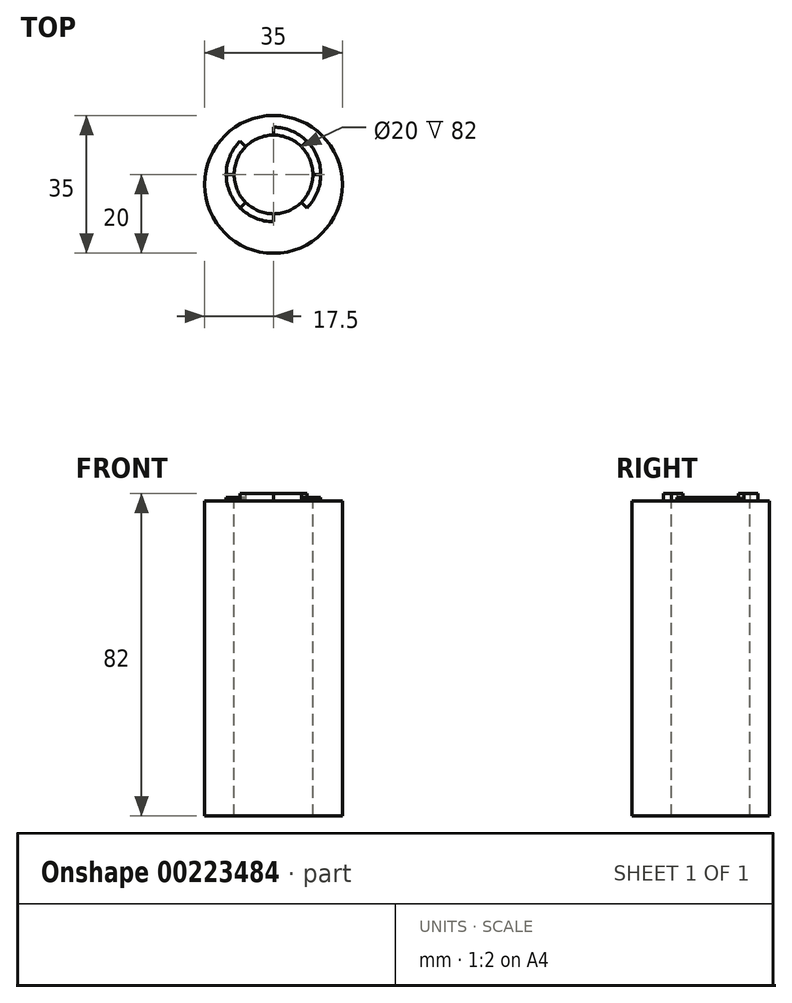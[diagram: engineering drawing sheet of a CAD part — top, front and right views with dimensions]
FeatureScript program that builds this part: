
annotation { "Feature Type Name" : "Feature", "Feature Type Description" : "" }
export const myFeature = defineFeature(function(context is Context, id is Id, definition is map)
    precondition{}
    {
        {
            assignVariable(context, id + "F0", {"name" : "TabDiameter", "anyValue" : 20 * mm});
        }
        {
            assignVariable(context, id + "F1", {"name" : "JigBaseHeight", "anyValue" : 80});
        }
        {
            var Q0;
            Q0=qCreatedBy(makeId("Top.planeOp"),FACE);
            var sketch = newSketch(context, id + "F2", { "sketchPlane" : qUnion([Q0])});
            skCircle(sketch, "E0", {"center": v(0, 0) * mm, "radius": 17.5 * mm});
            skSolve(sketch);
        }
        {
            var Q0;
            Q0 = qSketchRegion(id + "F2", true);
            extrude(context, id + "F3", {"entities" : qUnion([Q0]), "depth" : (getVariable(context, 'JigBaseHeight')) * mm});
        }
        {
            var Q0;
            Q0=makeQuery(id+"F3.opExtrude","CAP_FACE",FACE,{"disambiguationData":[OSD([sQuery(id+"F2.wireOp",EDGE,"E0")])],"isStart":false});
            cPlane(context, id + "F4", {"entities" : qUnion([Q0]), "cplaneType" : CPlaneType.OFFSET, "offset" : 0 * mm, "width" : 150 * mm, "height" : 150 * mm});
        }
        {
            var Q0;
            Q0=qCreatedBy(id+"F4.planeOp",FACE);
            var sketch = newSketch(context, id + "F5", { "sketchPlane" : qUnion([Q0])});
            skPoint(sketch, "E1", {"position": v(0, 2.5) * mm});
            skSolve(sketch);
        }
        {
            var Q0;
            Q0=sQuery(id+"F5.wireOp",VERTEX,"E1");
            var Q1;
            Q1=makeQuery(id+"F3.opExtrude","SWEPT_BODY",BODY,{"disambiguationData":[OSD([sQuery(id+"F2.wireOp",EDGE,"E0")])]});
            hole(context, id + "F6", {"style" : HoleStyle.SIMPLE, "endStyle" : HoleEndStyle.THROUGH, "holeDiameter" : getVariable(context, 'TabDiameter'), "locations" : qUnion([Q0]), "scope" : qUnion([Q1]), "isTappedThrough" : true});
        }
        {
            var Q0;
            Q0=qCreatedBy(id+"F4.planeOp",FACE);
            var sketch = newSketch(context, id + "F7", { "sketchPlane" : qUnion([Q0])});
            skPoint(sketch, "E2", {"position": v(0, 2.5) * mm});
            skArc(sketch, "E3", {"start": v(0, -7.5) * mm, "mid": v(3.83, -6.74) * mm, "end": v(7.07, -4.57) * mm, "construction": true});
            skLineSegment(sketch, "E4", {"start": v(0, -7.5) * mm, "end": v(0, 2.5) * mm, "construction": true});
            skLineSegment(sketch, "E5", {"start": v(7.07, -4.57) * mm, "end": v(0, 2.5) * mm, "construction": true});
            skArc(sketch, "E6", {"start": v(0, -7.5) * mm, "mid": v(-3.83, -6.74) * mm, "end": v(-7.07, -4.57) * mm});
            skLineSegment(sketch, "E7", {"start": v(-7.07, -4.57) * mm, "end": v(0, 2.5) * mm, "construction": true});
            skArc(sketch, "E8", {"start": v(-7.07, -4.57) * mm, "mid": v(-9.24, -1.33) * mm, "end": v(-10, 2.5) * mm, "construction": true});
            skArc(sketch, "E9", {"start": v(-10, 2.5) * mm, "mid": v(-9.24, 6.33) * mm, "end": v(-7.07, 9.57) * mm, "construction": true});
            skArc(sketch, "E10", {"start": v(-7.07, 9.57) * mm, "mid": v(-3.83, 11.74) * mm, "end": v(0, 12.5) * mm, "construction": true});
            skLineSegment(sketch, "E11", {"start": v(0, 2.5) * mm, "end": v(-10, 2.5) * mm, "construction": true});
            skLineSegment(sketch, "E12", {"start": v(0, 2.5) * mm, "end": v(-7.07, 9.57) * mm, "construction": true});
            skLineSegment(sketch, "E13", {"start": v(0, 2.5) * mm, "end": v(0, 12.5) * mm, "construction": true});
            skArc(sketch, "E14", {"start": v(0, 12.5) * mm, "mid": v(3.83, 11.74) * mm, "end": v(7.07, 9.57) * mm});
            skArc(sketch, "E15", {"start": v(7.07, 9.57) * mm, "mid": v(9.24, 6.33) * mm, "end": v(10, 2.5) * mm, "construction": true});
            skLineSegment(sketch, "E16", {"start": v(0, 2.5) * mm, "end": v(7.07, 9.57) * mm, "construction": true});
            skLineSegment(sketch, "E17", {"start": v(0, 2.5) * mm, "end": v(10, 2.5) * mm, "construction": true});
            skArc(sketch, "E18", {"start": v(0, -9.5) * mm, "mid": v(-4.6, -8.59) * mm, "end": v(-8.49, -5.99) * mm});
            skLineSegment(sketch, "E19", {"start": v(-8.49, -5.99) * mm, "end": v(0, 2.5) * mm, "construction": true});
            skLineSegment(sketch, "E20", {"start": v(0, -9.5) * mm, "end": v(0, 2.5) * mm, "construction": true});
            skLineSegment(sketch, "E21", {"start": v(0, 2.5) * mm, "end": v(-8.49, 10.99) * mm, "construction": true});
            skLineSegment(sketch, "E22", {"start": v(0, 2.5) * mm, "end": v(0, 14.43) * mm, "construction": true});
            skLineSegment(sketch, "E23", {"start": v(-8.49, -5.99) * mm, "end": v(-7.07, -4.57) * mm});
            skLineSegment(sketch, "E24", {"start": v(0, -7.5) * mm, "end": v(0, -9.5) * mm});
            skLineSegment(sketch, "E25", {"start": v(-7.07, 9.57) * mm, "end": v(-8.49, 10.99) * mm});
            skLineSegment(sketch, "E26", {"start": v(0, 12.5) * mm, "end": v(0, 14.43) * mm});
            skArc(sketch, "E27", {"start": v(0, 14.5) * mm, "mid": v(4.6, 13.59) * mm, "end": v(8.49, 10.99) * mm});
            skLineSegment(sketch, "E28", {"start": v(0, 14.5) * mm, "end": v(0, 2.5) * mm, "construction": true});
            skLineSegment(sketch, "E29", {"start": v(8.49, 10.99) * mm, "end": v(0, 2.5) * mm, "construction": true});
            skLineSegment(sketch, "E30", {"start": v(0, 14.5) * mm, "end": v(0, 12.5) * mm});
            skLineSegment(sketch, "E31", {"start": v(8.49, 10.99) * mm, "end": v(7.07, 9.57) * mm});
            skSolve(sketch);
        }
        {
            var Q0;
            Q0 = qSketchRegion(id + "F7", true);
            extrude(context, id + "F8", {"entities" : qUnion([Q0]), "operationType" : NewBodyOperationType.ADD, "depth" : 2 * mm});
        }
        {
            var Q0;
            Q0=qCreatedBy(id+"F4.planeOp",FACE);
            var sketch = newSketch(context, id + "F9", { "sketchPlane" : qUnion([Q0])});
            skPoint(sketch, "E32", {"position": v(0, 2.5) * mm});
            skArc(sketch, "E33", {"start": v(0, -7.5) * mm, "mid": v(3.83, -6.74) * mm, "end": v(7.07, -4.57) * mm, "construction": true});
            skLineSegment(sketch, "E34", {"start": v(0, -7.5) * mm, "end": v(0, 2.5) * mm, "construction": true});
            skLineSegment(sketch, "E35", {"start": v(7.07, -4.57) * mm, "end": v(0, 2.5) * mm, "construction": true});
            skArc(sketch, "E36", {"start": v(0, -7.5) * mm, "mid": v(-3.83, -6.74) * mm, "end": v(-7.07, -4.57) * mm});
            skLineSegment(sketch, "E37", {"start": v(-7.07, -4.57) * mm, "end": v(0, 2.5) * mm, "construction": true});
            skArc(sketch, "E38", {"start": v(-7.07, -4.57) * mm, "mid": v(-9.24, -1.33) * mm, "end": v(-10, 2.5) * mm});
            skArc(sketch, "E39", {"start": v(-10, 2.5) * mm, "mid": v(-9.24, 6.33) * mm, "end": v(-7.07, 9.57) * mm});
            skArc(sketch, "E40", {"start": v(-7.07, 9.57) * mm, "mid": v(-3.83, 11.74) * mm, "end": v(0, 12.5) * mm});
            skLineSegment(sketch, "E41", {"start": v(0, 2.5) * mm, "end": v(-10, 2.5) * mm, "construction": true});
            skLineSegment(sketch, "E42", {"start": v(0, 2.5) * mm, "end": v(-7.07, 9.57) * mm, "construction": true});
            skLineSegment(sketch, "E43", {"start": v(0, 2.5) * mm, "end": v(0, 12.5) * mm, "construction": true});
            skArc(sketch, "E44", {"start": v(7.07, 9.57) * mm, "mid": v(9.24, 6.33) * mm, "end": v(10, 2.5) * mm});
            skLineSegment(sketch, "E45", {"start": v(0, 2.5) * mm, "end": v(7.07, 9.57) * mm, "construction": true});
            skLineSegment(sketch, "E46", {"start": v(0, 2.5) * mm, "end": v(10, 2.5) * mm, "construction": true});
            skArc(sketch, "E47", {"start": v(-8.49, -5.99) * mm, "mid": v(-11.09, -2.1) * mm, "end": v(-12, 2.5) * mm});
            skLineSegment(sketch, "E48", {"start": v(-8.49, -5.99) * mm, "end": v(0, 2.5) * mm, "construction": true});
            skLineSegment(sketch, "E49", {"start": v(-12, 2.5) * mm, "end": v(0, 2.5) * mm, "construction": true});
            skLineSegment(sketch, "E50", {"start": v(-8.49, -5.99) * mm, "end": v(-7.07, -4.57) * mm});
            skLineSegment(sketch, "E51", {"start": v(-10, 2.5) * mm, "end": v(-12, 2.5) * mm});
            skPoint(sketch, "E52.startSnap0", {"position": v(-3.54, 6.04) * mm});
            skLineSegment(sketch, "E53", {"start": v(8.43, 10.93) * mm, "end": v(0, 2.5) * mm, "construction": true});
            skLineSegment(sketch, "E54", {"start": v(0, 14.5) * mm, "end": v(0, 2.5) * mm, "construction": true});
            skLineSegment(sketch, "E55", {"start": v(0, 14.5) * mm, "end": v(0, 12.5) * mm});
            skLineSegment(sketch, "E56", {"start": v(7.07, 9.57) * mm, "end": v(8.43, 10.93) * mm});
            skArc(sketch, "E57", {"start": v(8.49, 10.99) * mm, "mid": v(11.09, 7.1) * mm, "end": v(12, 2.5) * mm});
            skLineSegment(sketch, "E58", {"start": v(8.49, 10.99) * mm, "end": v(0, 2.5) * mm, "construction": true});
            skLineSegment(sketch, "E59", {"start": v(12, 2.5) * mm, "end": v(0, 2.5) * mm, "construction": true});
            skLineSegment(sketch, "E60", {"start": v(12, 2.5) * mm, "end": v(10, 2.5) * mm});
            skLineSegment(sketch, "E61", {"start": v(8.49, 10.99) * mm, "end": v(7.07, 9.57) * mm});
            skSolve(sketch);
        }
        {
            var Q0;
            Q0 = qSketchRegion(id + "F9", true);
            extrude(context, id + "F10", {"entities" : qUnion([Q0]), "operationType" : NewBodyOperationType.ADD, "depth" : .5 * mm});
        }
        {
            var Q0;
            Q0=qCreatedBy(id+"F4.planeOp",FACE);
            var sketch = newSketch(context, id + "F11", { "sketchPlane" : qUnion([Q0])});
            skPoint(sketch, "E62", {"position": v(0, 2.5) * mm});
            skArc(sketch, "E63", {"start": v(0, -7.5) * mm, "mid": v(3.83, -6.74) * mm, "end": v(7.07, -4.57) * mm, "construction": true});
            skLineSegment(sketch, "E64", {"start": v(0, -7.5) * mm, "end": v(0, 2.5) * mm, "construction": true});
            skLineSegment(sketch, "E65", {"start": v(7.07, -4.57) * mm, "end": v(0, 2.5) * mm, "construction": true});
            skArc(sketch, "E66", {"start": v(0, -7.5) * mm, "mid": v(-3.83, -6.74) * mm, "end": v(-7.07, -4.57) * mm});
            skLineSegment(sketch, "E67", {"start": v(-7.07, -4.57) * mm, "end": v(0, 2.5) * mm, "construction": true});
            skArc(sketch, "E68", {"start": v(-7.07, -4.57) * mm, "mid": v(-9.24, -1.33) * mm, "end": v(-10, 2.5) * mm});
            skArc(sketch, "E69", {"start": v(-10, 2.5) * mm, "mid": v(-9.24, 6.33) * mm, "end": v(-7.07, 9.57) * mm});
            skArc(sketch, "E70", {"start": v(-7.07, 9.57) * mm, "mid": v(-3.83, 11.74) * mm, "end": v(0, 12.5) * mm});
            skLineSegment(sketch, "E71", {"start": v(0, 2.5) * mm, "end": v(-10, 2.5) * mm, "construction": true});
            skLineSegment(sketch, "E72", {"start": v(0, 2.5) * mm, "end": v(-7.07, 9.57) * mm, "construction": true});
            skLineSegment(sketch, "E73", {"start": v(0, 2.5) * mm, "end": v(0, 12.5) * mm, "construction": true});
            skArc(sketch, "E74", {"start": v(0, 12.5) * mm, "mid": v(3.83, 11.74) * mm, "end": v(7.07, 9.57) * mm});
            skArc(sketch, "E75", {"start": v(7.07, 9.57) * mm, "mid": v(9.24, 6.33) * mm, "end": v(10, 2.5) * mm});
            skLineSegment(sketch, "E76", {"start": v(0, 2.5) * mm, "end": v(7.07, 9.57) * mm, "construction": true});
            skLineSegment(sketch, "E77", {"start": v(0, 2.5) * mm, "end": v(10, 2.5) * mm, "construction": true});
            skArc(sketch, "E78", {"start": v(-12, 2.5) * mm, "mid": v(-11.09, 7.1) * mm, "end": v(-8.49, 10.99) * mm});
            skLineSegment(sketch, "E79", {"start": v(-12, 2.5) * mm, "end": v(0, 2.5) * mm, "construction": true});
            skLineSegment(sketch, "E80", {"start": v(-8.49, 10.99) * mm, "end": v(0, 2.5) * mm, "construction": true});
            skLineSegment(sketch, "E81", {"start": v(8.49, 10.99) * mm, "end": v(0, 2.5) * mm, "construction": true});
            skLineSegment(sketch, "E82", {"start": v(8.49, -5.99) * mm, "end": v(0, 2.5) * mm, "construction": true});
            skLineSegment(sketch, "E83", {"start": v(-8.49, 10.99) * mm, "end": v(-7.07, 9.57) * mm});
            skLineSegment(sketch, "E84", {"start": v(-10, 2.5) * mm, "end": v(-12, 2.5) * mm});
            skLineSegment(sketch, "E85", {"start": v(7.07, -4.57) * mm, "end": v(8.49, -5.99) * mm});
            skLineSegment(sketch, "E86", {"start": v(7.07, 9.57) * mm, "end": v(8.49, 10.99) * mm});
            skArc(sketch, "E87", {"start": v(12, 2.5) * mm, "mid": v(11.09, -2.1) * mm, "end": v(8.49, -5.99) * mm});
            skLineSegment(sketch, "E88", {"start": v(12, 2.5) * mm, "end": v(0, 2.5) * mm, "construction": true});
            skArc(sketch, "E89", {"start": v(7.07, -4.57) * mm, "mid": v(9.24, -1.33) * mm, "end": v(10, 2.5) * mm});
            skLineSegment(sketch, "E90", {"start": v(12, 2.5) * mm, "end": v(10, 2.5) * mm});
            skLineSegment(sketch, "E91", {"start": v(8.49, -5.99) * mm, "end": v(7.07, -4.57) * mm});
            skSolve(sketch);
        }
        {
            var Q0;
            Q0 = qSketchRegion(id + "F11", true);
            extrude(context, id + "F12", {"entities" : qUnion([Q0]), "operationType" : NewBodyOperationType.ADD, "depth" : 1 * mm});
        }
    });
